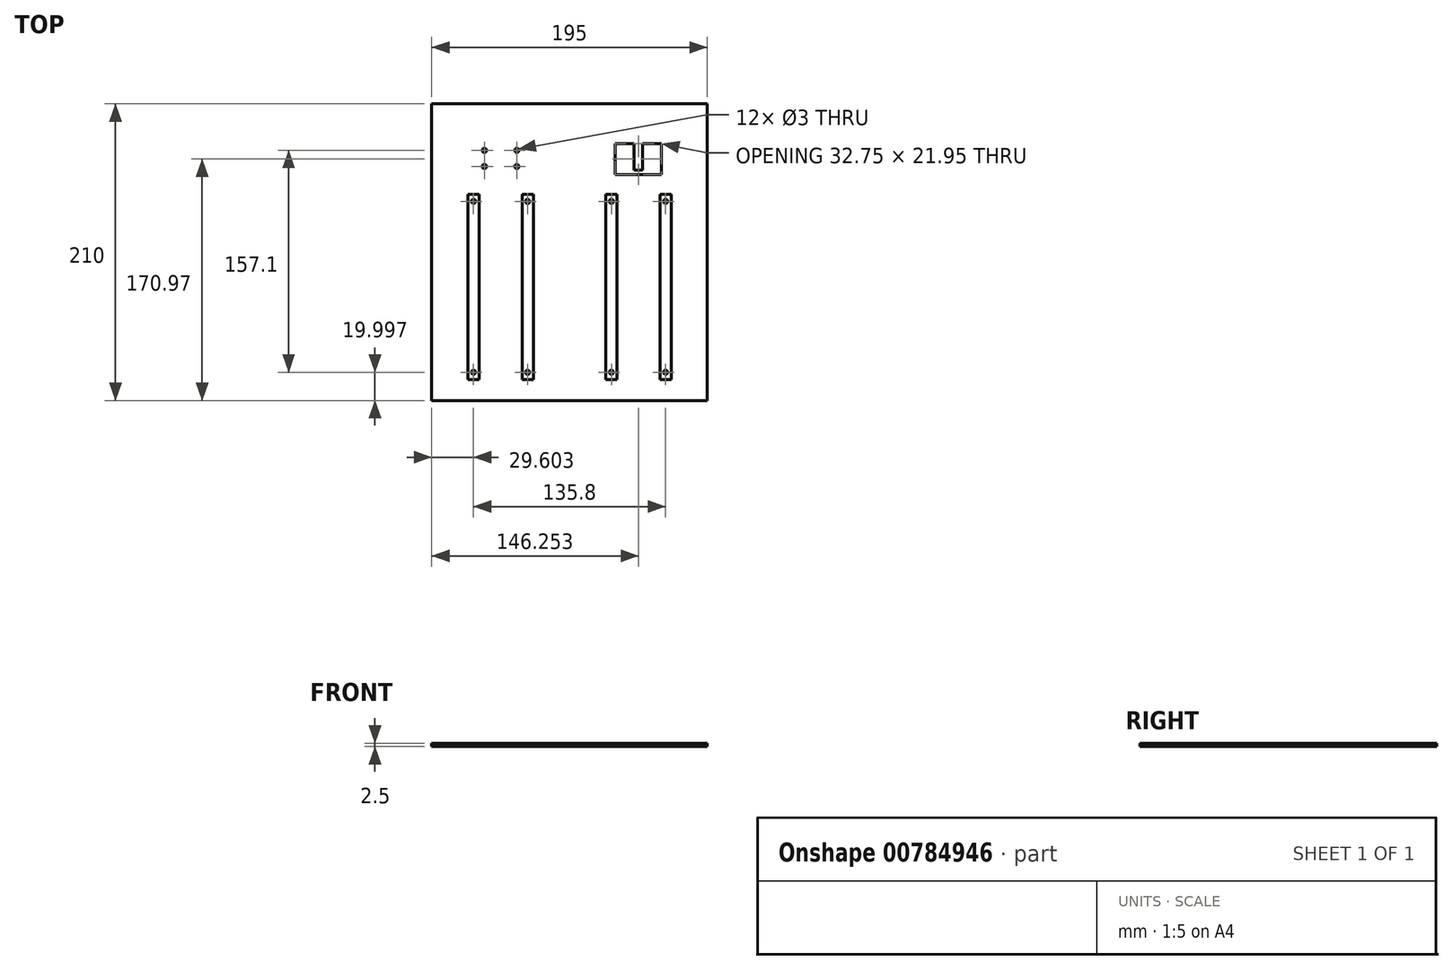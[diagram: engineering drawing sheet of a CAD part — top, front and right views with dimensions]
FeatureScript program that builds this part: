
annotation { "Feature Type Name" : "Feature", "Feature Type Description" : "" }
export const myFeature = defineFeature(function(context is Context, id is Id, definition is map)
    precondition{}
    {
        {
            var Q0;
            Q0=qCreatedBy(makeId("Top.planeOp"),FACE);
            var sketch = newSketch(context, id + "F0", { "sketchPlane" : qUnion([Q0])});
            skPoint(sketch, "E0.0", {"position": v(1.37, -100.22) * mm});
            skPoint(sketch, "E1.0", {"position": v(1.37, 109.78) * mm});
            skLineSegment(sketch, "E2", {"start": v(1.37, 109.78) * mm, "end": v(1.37, -83.97) * mm, "construction": true});
            skLineSegment(sketch, "E3.bottom", {"start": v(15.87, 109.78) * mm, "end": v(-13.13, 109.78) * mm});
            skPoint(sketch, "E4.middle", {"position": v(1.37, 47.28) * mm});
            skPoint(sketch, "E5.middle", {"position": v(1.37, -83.97) * mm});
            skLineSegment(sketch, "E6.left", {"start": v(-13.78, -75.22) * mm, "end": v(-13.78, -39.22) * mm});
            skPoint(sketch, "E6.middle", {"position": v(1.37, -58.22) * mm});
            skPoint(sketch, "E7.middle", {"position": v(1.37, -36.72) * mm});
            skLineSegment(sketch, "E8.bottom", {"start": v(-13.78, 35.78) * mm, "end": v(-21.78, 35.78) * mm, "construction": true});
            skLineSegment(sketch, "E8.top", {"start": v(-13.78, -85.22) * mm, "end": v(-21.78, -85.22) * mm});
            skLineSegment(sketch, "E8.left", {"start": v(-13.78, 35.78) * mm, "end": v(-13.78, -85.22) * mm});
            skLineSegment(sketch, "E8.right", {"start": v(-21.78, 35.78) * mm, "end": v(-21.78, -85.22) * mm});
            skPoint(sketch, "E8.middle", {"position": v(-17.78, -24.72) * mm});
            skLineSegment(sketch, "E9.MirrorCS", {"start": v(16.52, 35.78) * mm, "end": v(16.52, -85.22) * mm});
            skLineSegment(sketch, "E10.MirrorCS", {"start": v(16.52, 35.78) * mm, "end": v(24.52, 35.78) * mm});
            skLineSegment(sketch, "E11.MirrorCS", {"start": v(24.52, 35.78) * mm, "end": v(24.52, -85.22) * mm});
            skLineSegment(sketch, "E12.MirrorCS", {"start": v(16.52, -85.22) * mm, "end": v(24.52, -85.22) * mm});
            skLineSegment(sketch, "E13", {"start": v(-13.78, 35.78) * mm, "end": v(-13.78, 45.78) * mm});
            skLineSegment(sketch, "E14", {"start": v(-13.78, 45.78) * mm, "end": v(-21.78, 45.78) * mm});
            skLineSegment(sketch, "E15", {"start": v(-21.78, 45.78) * mm, "end": v(-21.78, 35.78) * mm});
            skLineSegment(sketch, "E16.MirrorCS", {"start": v(16.52, 35.78) * mm, "end": v(16.52, 45.78) * mm});
            skLineSegment(sketch, "E17.MirrorCS", {"start": v(16.52, 45.78) * mm, "end": v(24.52, 45.78) * mm});
            skLineSegment(sketch, "E18.MirrorCS", {"start": v(24.52, 45.78) * mm, "end": v(24.52, 35.78) * mm});
            skCircle(sketch, "E19", {"center": v(-17.78, 40.78) * mm, "radius": 1.5 * mm});
            skLineSegment(sketch, "E20", {"start": v(-21.78, 45.78) * mm, "end": v(-13.78, 35.78) * mm, "construction": true});
            skLineSegment(sketch, "E21", {"start": v(-13.78, 45.78) * mm, "end": v(-21.78, 35.78) * mm, "construction": true});
            skCircle(sketch, "E22.MirrorC", {"center": v(20.52, 40.78) * mm, "radius": 1.5 * mm});
            skLineSegment(sketch, "E23.0", {"start": v(-20.63, 35.78) * mm, "end": v(-20.63, -75.22) * mm, "construction": true});
            skLineSegment(sketch, "E24.MirrorCS", {"start": v(23.37, 35.78) * mm, "end": v(23.37, -75.22) * mm, "construction": true});
            skLineSegment(sketch, "E25", {"start": v(-20.63, -39.22) * mm, "end": v(-20.63, -75.22) * mm});
            skLineSegment(sketch, "E26", {"start": v(23.37, -75.22) * mm, "end": v(23.37, -39.22) * mm});
            skLineSegment(sketch, "E27.0", {"start": v(-47.38, 109.78) * mm, "end": v(-47.38, -100.22) * mm});
            skLineSegment(sketch, "E28.0", {"start": v(50.12, 109.78) * mm, "end": v(50.12, -100.22) * mm});
            skLineSegment(sketch, "E29.0", {"start": v(50.12, 109.78) * mm, "end": v(-47.38, 109.78) * mm});
            skLineSegment(sketch, "E30.0", {"start": v(50.12, -100.22) * mm, "end": v(-47.38, -100.22) * mm});
            skLineSegment(sketch, "E31.top", {"start": v(-25.63, -100.22) * mm, "end": v(28.37, -100.22) * mm});
            skLineSegment(sketch, "E31.left", {"start": v(-25.63, 77.68) * mm, "end": v(-25.63, -100.22) * mm, "construction": true});
            skLineSegment(sketch, "E31.right", {"start": v(28.37, 77.68) * mm, "end": v(28.37, -100.22) * mm, "construction": true});
            skLineSegment(sketch, "E32", {"start": v(-21.78, 45.78) * mm, "end": v(-21.78, -85.22) * mm, "construction": true});
            skPoint(sketch, "E33", {"position": v(-21.78, -19.72) * mm});
            skCircle(sketch, "E34.MirrorC", {"center": v(-17.78, -80.22) * mm, "radius": 1.5 * mm});
            skLineSegment(sketch, "E35.MirrorCS", {"start": v(-13.78, -75.22) * mm, "end": v(-21.78, -75.22) * mm});
            skCircle(sketch, "E36.MirrorC", {"center": v(20.52, -80.22) * mm, "radius": 1.5 * mm});
            skLineSegment(sketch, "E37.MirrorCS", {"start": v(16.52, -75.22) * mm, "end": v(24.52, -75.22) * mm});
            skPoint(sketch, "E38.0", {"position": v(-37.4, 145.33) * mm});
            skLineSegment(sketch, "E39.0", {"start": v(-15, 81.72) * mm, "end": v(-15, 59.78) * mm});
            skLineSegment(sketch, "E40.0", {"start": v(-15, 81.72) * mm, "end": v(-1.63, 81.72) * mm});
            skLineSegment(sketch, "E41.0", {"start": v(-1.63, 81.72) * mm, "end": v(-1.63, 62.78) * mm});
            skLineSegment(sketch, "E42.0", {"start": v(4.37, 81.72) * mm, "end": v(4.37, 62.78) * mm});
            skLineSegment(sketch, "E43.0.0", {"start": v(-1.63, 81.72) * mm, "end": v(-15, 81.72) * mm});
            skLineSegment(sketch, "E43.0.2", {"start": v(-15, 59.78) * mm, "end": v(17.75, 59.78) * mm});
            skLineSegment(sketch, "E43.0.3", {"start": v(17.75, 59.78) * mm, "end": v(17.75, 81.72) * mm});
            skLineSegment(sketch, "E43.0.4", {"start": v(17.75, 81.72) * mm, "end": v(4.37, 81.72) * mm});
            skLineSegment(sketch, "E43.0.6", {"start": v(4.37, 62.78) * mm, "end": v(-1.63, 62.78) * mm});
            skLineSegment(sketch, "E43.0.7", {"start": v(-1.63, 62.78) * mm, "end": v(-1.63, 81.72) * mm});
            skCircle(sketch, "E44.0", {"center": v(-10.1, 65.48) * mm, "radius": 1.5 * mm});
            skCircle(sketch, "E45.0", {"center": v(-10.1, 76.88) * mm, "radius": 1.5 * mm});
            skCircle(sketch, "E46.0", {"center": v(12.85, 65.48) * mm, "radius": 1.5 * mm});
            skCircle(sketch, "E47.0", {"center": v(12.85, 76.88) * mm, "radius": 1.5 * mm});
            skLineSegment(sketch, "E48.0.2", {"start": v(-15, 59.78) * mm, "end": v(17.75, 59.78) * mm, "construction": true});
            skLineSegment(sketch, "E49", {"start": v(17.75, 59.78) * mm, "end": v(-15, 59.78) * mm});
            skLineSegment(sketch, "E50", {"start": v(17.75, 81.72) * mm, "end": v(17.75, 59.78) * mm});
            skLineSegment(sketch, "E51", {"start": v(-15, 59.78) * mm, "end": v(-15, 81.72) * mm});
            skPoint(sketch, "E52", {"position": v(1.37, 59.78) * mm});
            skPoint(sketch, "E53.trimOffspring.end.orphan", {"position": v(-15.48, -82.69) * mm});
            skLineSegment(sketch, "E54.trimOffspring", {"start": v(1.37, -92.72) * mm, "end": v(1.37, -100.22) * mm, "construction": true});
            skPoint(sketch, "E55.trimOffspring.end.orphan", {"position": v(18.22, -82.69) * mm});
            skPoint(sketch, "E56.orphan", {"position": v(0.48, -75.22) * mm});
            skPoint(sketch, "E5.top.start.orphan", {"position": v(-2.89, -75.22) * mm});
            skLineSegment(sketch, "E57.MirrorCS", {"start": v(95.87, 62.78) * mm, "end": v(101.87, 62.78) * mm});
            skLineSegment(sketch, "E58.MirrorCS", {"start": v(114.02, 35.78) * mm, "end": v(122.02, 35.78) * mm, "construction": true});
            skLineSegment(sketch, "E59.MirrorCS", {"start": v(83.72, 35.78) * mm, "end": v(75.72, 35.78) * mm});
            skLineSegment(sketch, "E60.MirrorCS", {"start": v(101.87, 81.72) * mm, "end": v(115.25, 81.72) * mm});
            skLineSegment(sketch, "E61.MirrorCS", {"start": v(114.02, 45.78) * mm, "end": v(122.02, 45.78) * mm});
            skLineSegment(sketch, "E62.MirrorCS", {"start": v(101.87, 62.78) * mm, "end": v(101.87, 81.72) * mm});
            skLineSegment(sketch, "E63.MirrorCS", {"start": v(82.5, 59.78) * mm, "end": v(82.5, 81.72) * mm});
            skLineSegment(sketch, "E64.MirrorCS", {"start": v(115.25, 59.78) * mm, "end": v(115.25, 81.72) * mm});
            skLineSegment(sketch, "E65.MirrorCS", {"start": v(95.87, 81.72) * mm, "end": v(95.87, 62.78) * mm});
            skLineSegment(sketch, "E66.MirrorCS", {"start": v(83.72, -85.22) * mm, "end": v(75.72, -85.22) * mm});
            skCircle(sketch, "E67.MirrorC", {"center": v(87.4, 65.48) * mm, "radius": 1.5 * mm});
            skLineSegment(sketch, "E68.MirrorCS", {"start": v(83.72, -75.22) * mm, "end": v(75.72, -75.22) * mm});
            skCircle(sketch, "E69.MirrorC", {"center": v(110.35, 65.48) * mm, "radius": 1.5 * mm});
            skLineSegment(sketch, "E70.MirrorCS", {"start": v(114.02, 45.78) * mm, "end": v(122.02, 35.78) * mm, "construction": true});
            skLineSegment(sketch, "E71.MirrorCS", {"start": v(115.25, 59.78) * mm, "end": v(82.5, 59.78) * mm});
            skCircle(sketch, "E72.MirrorC", {"center": v(110.35, 76.88) * mm, "radius": 1.5 * mm});
            skLineSegment(sketch, "E73.MirrorCS", {"start": v(83.72, 45.78) * mm, "end": v(75.72, 45.78) * mm});
            skLineSegment(sketch, "E74.MirrorCS", {"start": v(114.02, -75.22) * mm, "end": v(122.02, -75.22) * mm});
            skCircle(sketch, "E75.MirrorC", {"center": v(87.4, 76.88) * mm, "radius": 1.5 * mm});
            skLineSegment(sketch, "E76.MirrorCS", {"start": v(122.02, 45.78) * mm, "end": v(114.02, 35.78) * mm, "construction": true});
            skLineSegment(sketch, "E77.MirrorCS", {"start": v(82.5, 81.72) * mm, "end": v(95.87, 81.72) * mm});
            skPoint(sketch, "E78.MirrorP", {"position": v(98.87, -100.22) * mm});
            skLineSegment(sketch, "E79.MirrorCS", {"start": v(101.87, 81.72) * mm, "end": v(101.87, 62.78) * mm});
            skLineSegment(sketch, "E80.MirrorCS", {"start": v(115.25, 81.72) * mm, "end": v(115.25, 59.78) * mm});
            skLineSegment(sketch, "E81.MirrorCS", {"start": v(82.5, 81.72) * mm, "end": v(82.5, 59.78) * mm});
            skPoint(sketch, "E82.MirrorP", {"position": v(98.87, 59.78) * mm});
            skLineSegment(sketch, "E83.MirrorCS", {"start": v(115.25, 81.72) * mm, "end": v(101.87, 81.72) * mm});
            skCircle(sketch, "E84.MirrorC", {"center": v(79.72, -80.22) * mm, "radius": 1.5 * mm});
            skLineSegment(sketch, "E85.MirrorCS", {"start": v(122.02, 35.78) * mm, "end": v(122.02, -85.22) * mm});
            skLineSegment(sketch, "E86.MirrorCS", {"start": v(82.5, 59.78) * mm, "end": v(115.25, 59.78) * mm});
            skLineSegment(sketch, "E87.MirrorCS", {"start": v(114.02, -85.22) * mm, "end": v(122.02, -85.22) * mm});
            skLineSegment(sketch, "E88.MirrorCS", {"start": v(120.87, -39.22) * mm, "end": v(120.87, -75.22) * mm});
            skPoint(sketch, "E89.MirrorP", {"position": v(98.87, 109.78) * mm});
            skLineSegment(sketch, "E90.MirrorCS", {"start": v(114.02, -75.22) * mm, "end": v(114.02, -39.22) * mm});
            skLineSegment(sketch, "E91.MirrorCS", {"start": v(98.87, -92.72) * mm, "end": v(98.87, -100.22) * mm, "construction": true});
            skCircle(sketch, "E92.MirrorC", {"center": v(79.72, 40.78) * mm, "radius": 1.5 * mm});
            skLineSegment(sketch, "E93.MirrorCS", {"start": v(122.02, 45.78) * mm, "end": v(122.02, 35.78) * mm});
            skCircle(sketch, "E94.MirrorC", {"center": v(118.02, -80.22) * mm, "radius": 1.5 * mm});
            skLineSegment(sketch, "E95.MirrorCS", {"start": v(76.87, -75.22) * mm, "end": v(76.87, -39.22) * mm});
            skCircle(sketch, "E96.MirrorC", {"center": v(118.02, 40.78) * mm, "radius": 1.5 * mm});
            skLineSegment(sketch, "E97.MirrorCS", {"start": v(114.02, 35.78) * mm, "end": v(114.02, 45.78) * mm});
            skLineSegment(sketch, "E98.MirrorCS", {"start": v(75.72, 35.78) * mm, "end": v(75.72, -85.22) * mm});
            skLineSegment(sketch, "E99.MirrorCS", {"start": v(75.72, 45.78) * mm, "end": v(75.72, 35.78) * mm});
            skLineSegment(sketch, "E100.MirrorCS", {"start": v(83.72, 35.78) * mm, "end": v(83.72, -85.22) * mm});
            skLineSegment(sketch, "E101.MirrorCS", {"start": v(122.02, 45.78) * mm, "end": v(122.02, -85.22) * mm});
            skPoint(sketch, "E102.MirrorP", {"position": v(122.02, -19.72) * mm});
            skLineSegment(sketch, "E103.MirrorCS", {"start": v(114.02, 35.78) * mm, "end": v(114.02, -85.22) * mm});
            skLineSegment(sketch, "E104.MirrorCS", {"start": v(76.87, 35.78) * mm, "end": v(76.87, -75.22) * mm, "construction": true});
            skLineSegment(sketch, "E105.MirrorCS", {"start": v(71.87, 77.68) * mm, "end": v(71.87, -100.22) * mm, "construction": true});
            skPoint(sketch, "E106.MirrorP", {"position": v(98.87, -83.97) * mm});
            skLineSegment(sketch, "E107.MirrorCS", {"start": v(147.62, 109.78) * mm, "end": v(147.62, -100.22) * mm});
            skPoint(sketch, "E108.MirrorP", {"position": v(98.87, -36.72) * mm});
            skLineSegment(sketch, "E109.MirrorCS", {"start": v(84.37, 109.78) * mm, "end": v(113.37, 109.78) * mm});
            skPoint(sketch, "E110.MirrorP", {"position": v(115.72, -82.69) * mm});
            skLineSegment(sketch, "E111.MirrorCS", {"start": v(98.87, 109.78) * mm, "end": v(98.87, -83.97) * mm, "construction": true});
            skLineSegment(sketch, "E112.MirrorCS", {"start": v(50.12, 109.78) * mm, "end": v(147.62, 109.78) * mm});
            skPoint(sketch, "E113.MirrorP", {"position": v(99.76, -75.22) * mm});
            skLineSegment(sketch, "E114.MirrorCS", {"start": v(125.87, -100.22) * mm, "end": v(71.87, -100.22) * mm});
            skLineSegment(sketch, "E115.MirrorCS", {"start": v(83.72, 35.78) * mm, "end": v(83.72, 45.78) * mm});
            skLineSegment(sketch, "E116.MirrorCS", {"start": v(115.25, 59.78) * mm, "end": v(82.5, 59.78) * mm, "construction": true});
            skPoint(sketch, "E117.MirrorP", {"position": v(103.13, -75.22) * mm});
            skLineSegment(sketch, "E118.MirrorCS", {"start": v(120.87, 35.78) * mm, "end": v(120.87, -75.22) * mm, "construction": true});
            skLineSegment(sketch, "E119.MirrorCS", {"start": v(125.87, 77.68) * mm, "end": v(125.87, -100.22) * mm, "construction": true});
            skPoint(sketch, "E120.MirrorP", {"position": v(98.87, 47.28) * mm});
            skPoint(sketch, "E121.MirrorP", {"position": v(98.87, -58.22) * mm});
            skPoint(sketch, "E122.MirrorP", {"position": v(118.02, -24.72) * mm});
            skPoint(sketch, "E123.MirrorP", {"position": v(82.02, -82.69) * mm});
            skLineSegment(sketch, "E124.MirrorCS", {"start": v(50.12, -100.22) * mm, "end": v(147.62, -100.22) * mm});
            skLineSegment(sketch, "E125", {"start": v(-13.78, -75.22) * mm, "end": v(-21.78, -85.22) * mm, "construction": true});
            skLineSegment(sketch, "E126", {"start": v(24.52, -75.22) * mm, "end": v(16.52, -85.22) * mm, "construction": true});
            skLineSegment(sketch, "E127", {"start": v(-21.78, -75.22) * mm, "end": v(-13.78, -85.22) * mm, "construction": true});
            skLineSegment(sketch, "E128", {"start": v(16.52, -75.22) * mm, "end": v(24.52, -85.22) * mm, "construction": true});
            skSolve(sketch);
        }
        {
            var Q0;
            Q0=makeQuery(id+"F0.imprint","IMPRINT",FACE,{"disambiguationData":[TD([[makeQuery(id+"F0.imprint","IMPRINT",EDGE,{"derivedFrom":sQuery(id+"F0.wireOp",EDGE,"E44.0")}),-1.0]])]});
            var Q1;
            {var subQ0=sQuery(id+"F0.wireOp",EDGE,"E28.0");Q1=makeQuery(id+"F0.imprint","IMPRINT",FACE,{"disambiguationData":[TD([[makeQuery(id+"F0.imprint","IMPRINT",EDGE,{"derivedFrom":subQ0}),1.0]])]});}
            var Q2;
            Q2=makeQuery(id+"F0.imprint","IMPRINT",FACE,{"disambiguationData":[TD([[makeQuery(id+"F0.imprint","IMPRINT",EDGE,{"derivedFrom":sQuery(id+"F0.wireOp",EDGE,"E57.MirrorCS")}),-1.0]])]});
            var Q3;
            {var subQ9=sQuery(id+"F0.wireOp",EDGE,"E8.top");Q3=makeQuery(id+"F0.imprint","IMPRINT",FACE,{"disambiguationData":[TD([[makeQuery(id+"F0.imprint","IMPRINT",EDGE,{"derivedFrom":subQ9}),1.0]])]});}
            extrude(context, id + "F1", {"entities" : qUnion([Q0, Q1, Q2, Q3]), "depth" : 2.5 * mm, "offsetDistance" : 25 * mm});
        }
        {
            var Q0;
            {var subQ4=sQuery(id+"F0.wireOp",EDGE,"E13");Q0=makeQuery(id+"F0.imprint","IMPRINT",FACE,{"disambiguationData":[TD([[makeQuery(id+"F0.imprint","IMPRINT",EDGE,{"derivedFrom":subQ4}),1.0]])]});}
            var Q1;
            {var subQ1=sQuery(id+"F0.wireOp",EDGE,"E8.top");Q1=makeQuery(id+"F0.imprint","IMPRINT",FACE,{"disambiguationData":[TD([[makeQuery(id+"F0.imprint","IMPRINT",EDGE,{"derivedFrom":subQ1}),-1.0]])]});}
            var Q2;
            {var subQ4=sQuery(id+"F0.wireOp",EDGE,"E10.MirrorCS");Q2=makeQuery(id+"F0.imprint","IMPRINT",FACE,{"disambiguationData":[TD([[makeQuery(id+"F0.imprint","IMPRINT",EDGE,{"derivedFrom":subQ4}),-1.0]])]});}
            var Q3;
            {var subQ0=sQuery(id+"F0.wireOp",EDGE,"E12.MirrorCS");Q3=makeQuery(id+"F0.imprint","IMPRINT",FACE,{"disambiguationData":[TD([[makeQuery(id+"F0.imprint","IMPRINT",EDGE,{"derivedFrom":subQ0}),1.0]])]});}
            var Q4;
            Q4=makeQuery(id+"F0.imprint","IMPRINT",FACE,{"disambiguationData":[TD([[makeQuery(id+"F0.imprint","IMPRINT",EDGE,{"derivedFrom":sQuery(id+"F0.wireOp",EDGE,"E10.MirrorCS")}),1.0]])]});
            var Q5;
            Q5=makeQuery(id+"F0.imprint","IMPRINT",FACE,{"disambiguationData":[TD([[makeQuery(id+"F0.imprint","IMPRINT",EDGE,{"derivedFrom":sQuery(id+"F0.wireOp",EDGE,"E59.MirrorCS")}),-1.0]])]});
            var Q6;
            {var subQ1=sQuery(id+"F0.wireOp",EDGE,"E59.MirrorCS");Q6=makeQuery(id+"F0.imprint","IMPRINT",FACE,{"disambiguationData":[TD([[makeQuery(id+"F0.imprint","IMPRINT",EDGE,{"derivedFrom":subQ1}),1.0]])]});}
            var Q7;
            {var subQ6=sQuery(id+"F0.wireOp",EDGE,"E66.MirrorCS");Q7=makeQuery(id+"F0.imprint","IMPRINT",FACE,{"disambiguationData":[TD([[makeQuery(id+"F0.imprint","IMPRINT",EDGE,{"derivedFrom":subQ6}),-1.0]])]});}
            var Q8;
            {var subQ4=sQuery(id+"F0.wireOp",EDGE,"E87.MirrorCS");Q8=makeQuery(id+"F0.imprint","IMPRINT",FACE,{"disambiguationData":[TD([[makeQuery(id+"F0.imprint","IMPRINT",EDGE,{"derivedFrom":subQ4}),1.0]])]});}
            var Q9;
            {var subQ8=sQuery(id+"F0.wireOp",EDGE,"E61.MirrorCS");Q9=makeQuery(id+"F0.imprint","IMPRINT",FACE,{"disambiguationData":[TD([[makeQuery(id+"F0.imprint","IMPRINT",EDGE,{"derivedFrom":subQ8}),-1.0]])]});}
            extrude(context, id + "F2", {"entities" : qUnion([Q0, Q1, Q2, Q3, Q4, Q5, Q6, Q7, Q8, Q9]), "operationType" : NewBodyOperationType.ADD, "depth" : 1.5 * mm, "offsetDistance" : 25 * mm});
        }
    });
